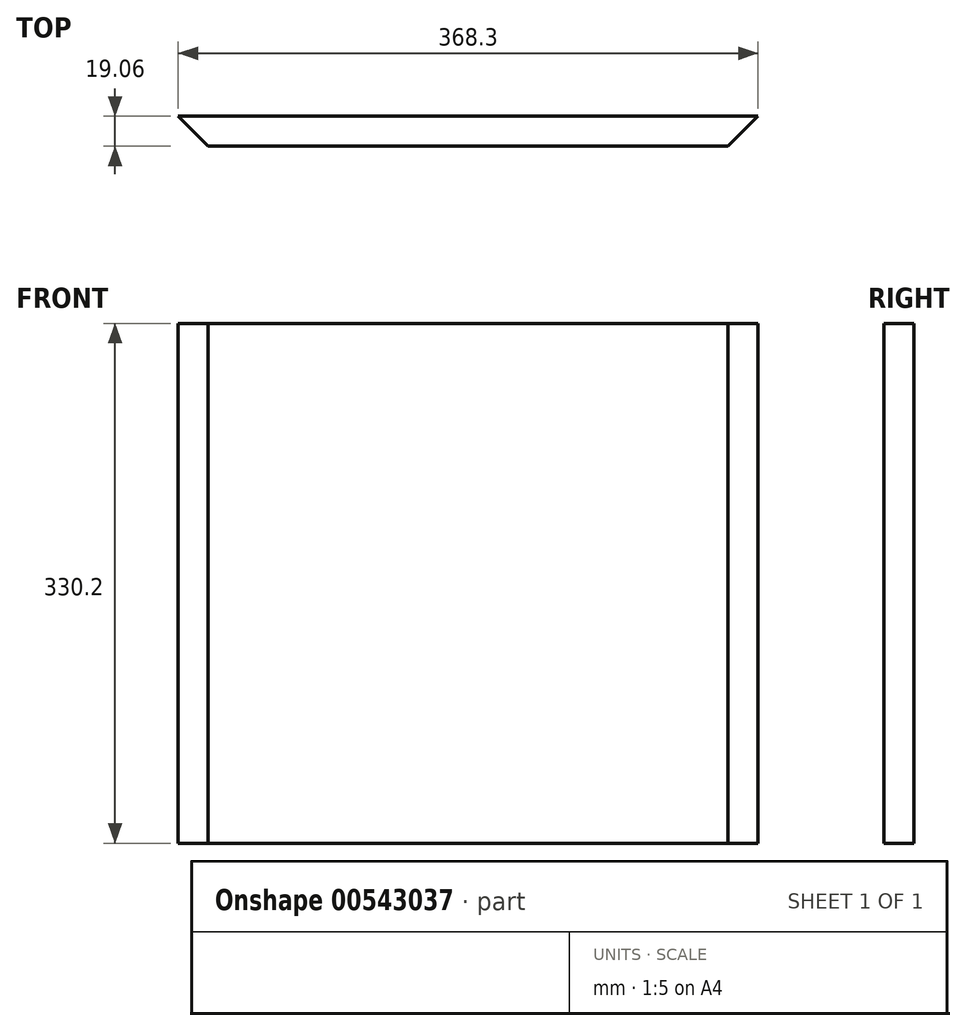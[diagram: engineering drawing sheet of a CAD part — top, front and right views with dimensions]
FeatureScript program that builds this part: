
annotation { "Feature Type Name" : "Feature", "Feature Type Description" : "" }
export const myFeature = defineFeature(function(context is Context, id is Id, definition is map)
    precondition{}
    {
        {
            var Q0;
            Q0=qCreatedBy(makeId("Top.planeOp"),FACE);
            var sketch = newSketch(context, id + "F0", { "sketchPlane" : qUnion([Q0])});
            skLineSegment(sketch, "E0", {"start": v(0, 9.53) * mm, "end": v(0, 0) * mm});
            skLineSegment(sketch, "E1", {"start": v(0, 0) * mm, "end": v(0, -9.53) * mm});
            skLineSegment(sketch, "E2", {"start": v(0, 9.53) * mm, "end": v(-184.15, 9.52) * mm});
            skLineSegment(sketch, "E3", {"start": v(-184.15, 9.52) * mm, "end": v(-165.1, -9.53) * mm});
            skLineSegment(sketch, "E4", {"start": v(-165.1, -9.53) * mm, "end": v(0, -9.53) * mm});
            skLineSegment(sketch, "E5.MirrorCS", {"start": v(0, 9.52) * mm, "end": v(184.15, 9.53) * mm});
            skLineSegment(sketch, "E6.MirrorCS", {"start": v(184.15, 9.53) * mm, "end": v(165.1, -9.52) * mm});
            skLineSegment(sketch, "E7.MirrorCS", {"start": v(165.1, -9.52) * mm, "end": v(0, -9.53) * mm});
            skSolve(sketch);
        }
        {
            var Q0;
            Q0 = qSketchRegion(id + "F0", true);
            extrude(context, id + "F1", {"entities" : qUnion([Q0]), "depth" : 330.2 * mm, "offsetDistance" : 25.4 * mm});
        }
    });
